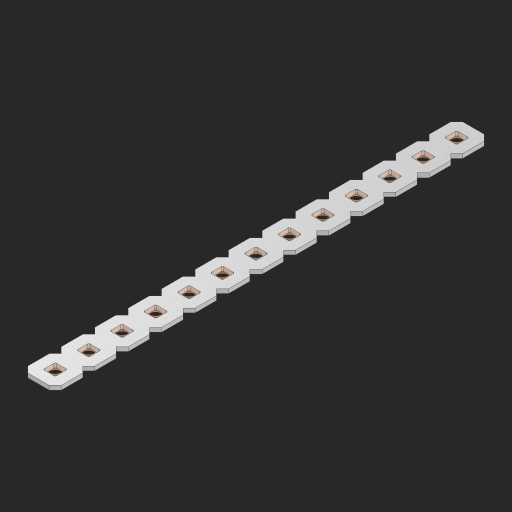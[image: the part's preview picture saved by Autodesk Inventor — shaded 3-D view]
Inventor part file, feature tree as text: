
AUTODESK INVENTOR PART (.ipt)
format: ipt  version: 2023 (Build 270158000, 158)  size: 408,576 bytes
history: native  units: in
note: dims shown in document units (in); Inventor stores cm internally (conversion verified against a paired STEP export)
features: other x14, extrude x12, sketch x2, pattern_linear x1
ambient origin geometry x8: Origin, YZ Plane, XZ Plane, XY Plane, X Axis, Y Axis, Z Axis, Center Point
bodies: Solid1 (feature_tree), Body (feature_tree)
feature tree (29):
  pattern_linear  "Rectangular Pattern1"  Spacing1=0.09in  [1 undecoded]
  sketch  "Sketch1"  dims[d1=0.5in]
  sketch  "Sketch2"  dims[d2=0.182in d3=0.09in d4=0.09in d5=0.09in d6=0.09in d7=0.09in d8=0.09in d9=0.09in d10=0.09in d11=0.02in d13=0.0in d14=0.172in d15=0.0625in d16=0.0in d19=0.5in d22=0.5in]
  other  "Srf1"
  other  "Srf126"
  other  "Srf127"
  other  "Srf128"
  other  "Srf129"
  other  "Srf130"
  other  "Srf131"
  other  "Srf250"
  other  "Srf251"
  other  "Srf252"
  other  "Srf253"
  other  "Srf254"
  other  "Srf255"
  other  "Circle"
  extrude  "ExtrusionSrf126"  Depth=0.09in
  extrude  "ExtrusionSrf127"  Depth=0.09in
  extrude  "ExtrusionSrf128"  Depth=0.09in
  extrude  "ExtrusionSrf129"  Depth=0.09in
  extrude  "ExtrusionSrf130"  Depth=0.09in
  extrude  "ExtrusionSrf131"  Depth=0.09in
  extrude  "ExtrusionSrf250"  Depth=0.09in
  extrude  "ExtrusionSrf251"  Depth=0.02in
  extrude  "ExtrusionSrf252"  TaperAngle=0.0deg  [1 undecoded]
  extrude  "ExtrusionSrf253"  Depth=0.5in
  extrude  "ExtrusionSrf254"  Depth=0.0625in TaperAngle=0.0deg
  extrude  "ExtrusionSrf255"  Depth=0.5in
note: 2 required parameter values undecoded (feature->parameter linkage not recoverable at this tier; creation-order binding heuristic only, values carry confidence <= 0.55)
